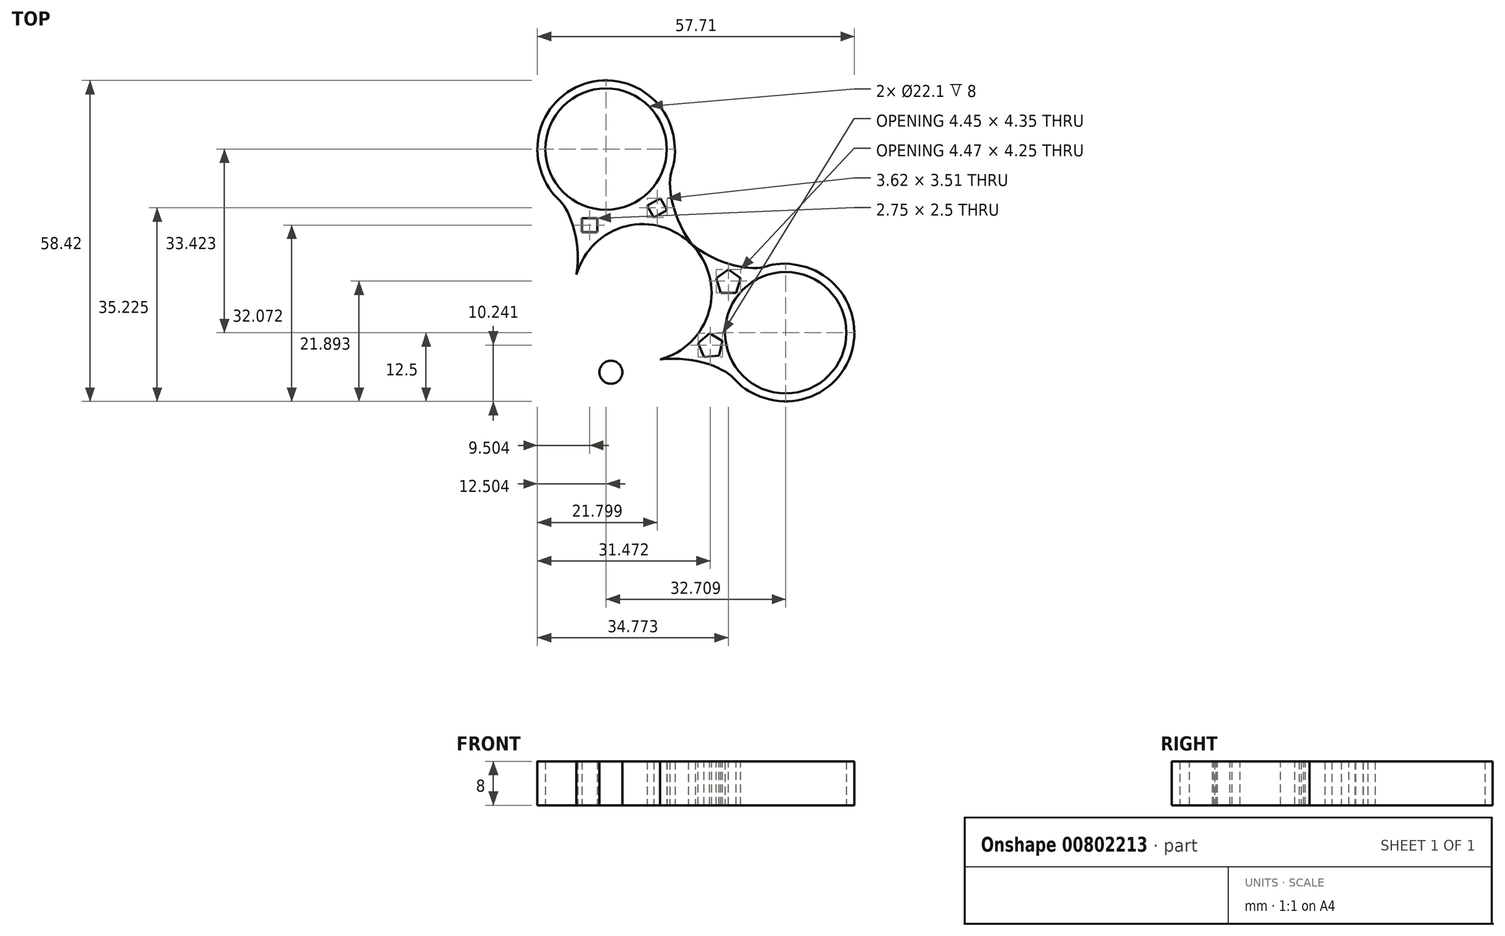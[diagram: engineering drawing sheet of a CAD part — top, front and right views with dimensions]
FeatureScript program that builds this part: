
annotation { "Feature Type Name" : "Feature", "Feature Type Description" : "" }
export const myFeature = defineFeature(function(context is Context, id is Id, definition is map)
    precondition{}
    {
        {
            var Q0;
            Q0=qCreatedBy(makeId("Top.planeOp"),FACE);
            var sketch = newSketch(context, id + "F0", { "sketchPlane" : qUnion([Q0])});
            skCircle(sketch, "E0", {"center": v(0, 0) * mm, "radius": 11.05 * mm});
            skCircle(sketch, "E1", {"center": v(-19.3, -18.88) * mm, "radius": 11.05 * mm});
            skArc(sketch, "E2", {"start": v(3.95, -11.86) * mm, "mid": v(8.93, 8.74) * mm, "end": v(-11.77, 4.2) * mm});
            skArc(sketch, "E3", {"start": v(-26.97, -9.02) * mm, "mid": v(-28.23, -27.63) * mm, "end": v(-9.6, -26.77) * mm});
            skFitSpline(sketch, "E4", {"points": [v(-11.77, 4.2) * mm, v(-20.67, -6.17) * mm, v(-26.97, -9.02) * mm], "startDerivative": vector(-9.98, -27.9) * mm, "endDerivative": vector(-24.04, -18.7) * mm});
            skLineSegment(sketch, "E5", {"start": v(0, 0) * mm, "end": v(-19.3, -18.88) * mm, "construction": true});
            skFitSpline(sketch, "E6.MirrorCS", {"points": [v(3.95, -11.86) * mm, v(-6.61, -20.53) * mm, v(-9.6, -26.77) * mm], "startDerivative": vector(-28.12, -9.37) * mm, "endDerivative": vector(-19.22, -23.63) * mm});
            skSolve(sketch);
        }
        {
            var Q0;
            Q0=makeQuery(id+"F0.imprint","IMPRINT",FACE,{"disambiguationData":[TD([[makeQuery(id+"F0.imprint","IMPRINT",EDGE,{"derivedFrom":sQuery(id+"F0.wireOp",EDGE,"E0")}),-1.0]])]});
            extrude(context, id + "F1", {"entities" : qUnion([Q0]), "depth" : 8 * mm, "offsetDistance" : 25 * mm});
        }
        {
            var Q0;
            Q0=makeQuery(id+"F1.opExtrude","SWEPT_BODY",BODY,{"disambiguationData":[OSD([sQuery(id+"F0.wireOp",EDGE,"E0"),sQuery(id+"F0.wireOp",EDGE,"E1"),sQuery(id+"F0.wireOp",EDGE,"E2"),sQuery(id+"F0.wireOp",EDGE,"E3"),sQuery(id+"F0.wireOp",EDGE,"E4"),sQuery(id+"F0.wireOp",EDGE,"E6.MirrorCS")])]});
            var Q1;
            Q1=makeQuery(id+"F1.opExtrude","CAP_EDGE",EDGE,{"disambiguationData":[OSD([sQuery(id+"F0.wireOp",EDGE,"E0")])],"isStart":true});
            circularPattern(context, id + "F2", {"entities" : qUnion([Q0]), "axis" : qUnion([Q1]), "angle" : 360 * degree, "instanceCount" : 3, "equalSpace" : true});
        }
        {
            var Q0;
            Q0=makeQuery(id+"F1.opExtrude","CAP_FACE",FACE,{"disambiguationData":[OSD([sQuery(id+"F0.wireOp",EDGE,"E0"),sQuery(id+"F0.wireOp",EDGE,"E1"),sQuery(id+"F0.wireOp",EDGE,"E2"),sQuery(id+"F0.wireOp",EDGE,"E3"),sQuery(id+"F0.wireOp",EDGE,"E4"),sQuery(id+"F0.wireOp",EDGE,"E6.MirrorCS")])],"isStart":false});
            var sketch = newSketch(context, id + "F3", { "sketchPlane" : qUnion([Q0])});
            skCircle(sketch, "E7", {"center": v(-14.58, -5.5) * mm, "radius": 2.1 * mm});
            skLineSegment(sketch, "E8", {"start": v(0, 0) * mm, "end": v(-19.3, -18.88) * mm, "construction": true});
            skCircle(sketch, "E9.MirrorC", {"center": v(-5.82, -14.46) * mm, "radius": 2.1 * mm});
            skSolve(sketch);
        }
        {
            var Q0;
            Q0=makeQuery(id+"F3.imprint","IMPRINT",FACE,{"disambiguationData":[TD([[makeQuery(id+"F3.imprint","IMPRINT",EDGE,{"derivedFrom":sQuery(id+"F3.wireOp",EDGE,"E9.MirrorC")}),-1.0]])]});
            var Q1;
            Q1=makeQuery(id+"F3.imprint","IMPRINT",FACE,{"disambiguationData":[TD([[makeQuery(id+"F3.imprint","IMPRINT",EDGE,{"derivedFrom":sQuery(id+"F3.wireOp",EDGE,"E7")}),1.0]])]});
            extrude(context, id + "F4", {"entities" : qUnion([Q0, Q1]), "operationType" : NewBodyOperationType.REMOVE, "oppositeDirection" : true, "depth" : 14.1 * mm, "offsetDistance" : 25 * mm});
        }
        {
            var Q0;
            Q0=makeQuery(id+"F2.opPattern","COPY",FACE,{"derivedFrom":makeQuery(id+"F1.opExtrude","CAP_FACE",FACE,{"disambiguationData":[OSD([sQuery(id+"F0.wireOp",EDGE,"E0"),sQuery(id+"F0.wireOp",EDGE,"E1"),sQuery(id+"F0.wireOp",EDGE,"E2"),sQuery(id+"F0.wireOp",EDGE,"E3"),sQuery(id+"F0.wireOp",EDGE,"E4"),sQuery(id+"F0.wireOp",EDGE,"E6.MirrorCS")])],"isStart":false}),"instanceName":"1"});
            var sketch = newSketch(context, id + "F5", { "sketchPlane" : qUnion([Q0])});
            skCircle(sketch, "E10.cCircle", {"center": v(15.56, 1.9) * mm, "radius": 1.9 * mm, "construction": true});
            skLineSegment(sketch, "E10.0", {"start": v(16.94, 0) * mm, "end": v(14.18, 0) * mm});
            skLineSegment(sketch, "E10.1", {"start": v(14.18, 0) * mm, "end": v(13.33, 2.62) * mm});
            skLineSegment(sketch, "E10.2", {"start": v(13.33, 2.62) * mm, "end": v(15.56, 4.25) * mm});
            skLineSegment(sketch, "E10.3", {"start": v(15.56, 4.25) * mm, "end": v(17.8, 2.62) * mm});
            skLineSegment(sketch, "E10.4", {"start": v(17.8, 2.62) * mm, "end": v(16.94, 0) * mm});
            skPoint(sketch, "E10.0.midPoint", {"position": v(15.56, 0) * mm});
            skLineSegment(sketch, "E11", {"start": v(0, 0) * mm, "end": v(26, -7.27) * mm, "construction": true});
            skCircle(sketch, "E12.MirrorC", {"center": v(12.32, -9.7) * mm, "radius": 1.9 * mm, "construction": true});
            skLineSegment(sketch, "E13.MirrorCS", {"start": v(11.1, -11.7) * mm, "end": v(13.85, -11.47) * mm});
            skLineSegment(sketch, "E14.MirrorCS", {"start": v(13.85, -11.47) * mm, "end": v(14.49, -8.79) * mm});
            skPoint(sketch, "E15.MirrorP", {"position": v(13.3, -8.07) * mm});
            skLineSegment(sketch, "E16.MirrorCS", {"start": v(14.49, -8.79) * mm, "end": v(12.13, -7.36) * mm});
            skLineSegment(sketch, "E17.MirrorCS", {"start": v(12.13, -7.36) * mm, "end": v(10.04, -9.16) * mm});
            skLineSegment(sketch, "E18.MirrorCS", {"start": v(10.04, -9.16) * mm, "end": v(11.1, -11.7) * mm});
            skSolve(sketch);
        }
        {
            var Q0;
            Q0=makeQuery(id+"F5.imprint","IMPRINT",FACE,{"disambiguationData":[TD([[makeQuery(id+"F5.imprint","IMPRINT",EDGE,{"derivedFrom":sQuery(id+"F5.wireOp",EDGE,"E13.MirrorCS")}),1.0]])]});
            var Q1;
            Q1=makeQuery(id+"F5.imprint","IMPRINT",FACE,{"disambiguationData":[TD([[makeQuery(id+"F5.imprint","IMPRINT",EDGE,{"derivedFrom":sQuery(id+"F5.wireOp",EDGE,"E10.0")}),-1.0]])]});
            extrude(context, id + "F6", {"entities" : qUnion([Q0, Q1]), "operationType" : NewBodyOperationType.REMOVE, "oppositeDirection" : true, "depth" : 15.9 * mm, "offsetDistance" : 25 * mm});
        }
        {
            var Q0;
            Q0=makeQuery(id+"F2.opPattern","COPY",FACE,{"derivedFrom":makeQuery(id+"F1.opExtrude","CAP_FACE",FACE,{"disambiguationData":[OSD([sQuery(id+"F0.wireOp",EDGE,"E0"),sQuery(id+"F0.wireOp",EDGE,"E1"),sQuery(id+"F0.wireOp",EDGE,"E2"),sQuery(id+"F0.wireOp",EDGE,"E3"),sQuery(id+"F0.wireOp",EDGE,"E4"),sQuery(id+"F0.wireOp",EDGE,"E6.MirrorCS")])],"isStart":true}),"instanceName":"2"});
            var sketch = newSketch(context, id + "F7", { "sketchPlane" : qUnion([Q0])});
            skLineSegment(sketch, "E19.bottom", {"start": v(-8.33, -13.55) * mm, "end": v(-11.08, -13.55) * mm});
            skLineSegment(sketch, "E19.top", {"start": v(-8.33, -11.05) * mm, "end": v(-11.08, -11.05) * mm});
            skLineSegment(sketch, "E19.left", {"start": v(-8.33, -13.55) * mm, "end": v(-8.33, -11.05) * mm});
            skLineSegment(sketch, "E19.right", {"start": v(-11.08, -13.55) * mm, "end": v(-11.08, -11.05) * mm});
            skPoint(sketch, "E19.middle", {"position": v(-9.7, -12.3) * mm});
            skLineSegment(sketch, "E20", {"start": v(0, 0) * mm, "end": v(-6.7, -26.15) * mm, "construction": true});
            skPoint(sketch, "E21.MirrorP", {"position": v(2.59, -15.45) * mm});
            skLineSegment(sketch, "E22.MirrorCS", {"start": v(1.98, -13.7) * mm, "end": v(4.4, -15.02) * mm});
            skLineSegment(sketch, "E23.MirrorCS", {"start": v(0.78, -15.89) * mm, "end": v(1.98, -13.7) * mm});
            skLineSegment(sketch, "E24.MirrorCS", {"start": v(0.78, -15.89) * mm, "end": v(3.2, -17.21) * mm});
            skLineSegment(sketch, "E25.MirrorCS", {"start": v(3.2, -17.21) * mm, "end": v(4.4, -15.02) * mm});
            skSolve(sketch);
        }
        {
            var Q0;
            Q0=makeQuery(id+"F7.imprint","IMPRINT",FACE,{"disambiguationData":[TD([[makeQuery(id+"F7.imprint","IMPRINT",EDGE,{"derivedFrom":sQuery(id+"F7.wireOp",EDGE,"E19.bottom")}),-1.0]])]});
            var Q1;
            Q1=makeQuery(id+"F7.imprint","IMPRINT",FACE,{"disambiguationData":[TD([[makeQuery(id+"F7.imprint","IMPRINT",EDGE,{"derivedFrom":sQuery(id+"F7.wireOp",EDGE,"E22.MirrorCS")}),-1.0]])]});
            extrude(context, id + "F8", {"entities" : qUnion([Q0, Q1]), "operationType" : NewBodyOperationType.REMOVE, "oppositeDirection" : true, "depth" : 25 * mm, "offsetDistance" : 25 * mm});
        }
    });
